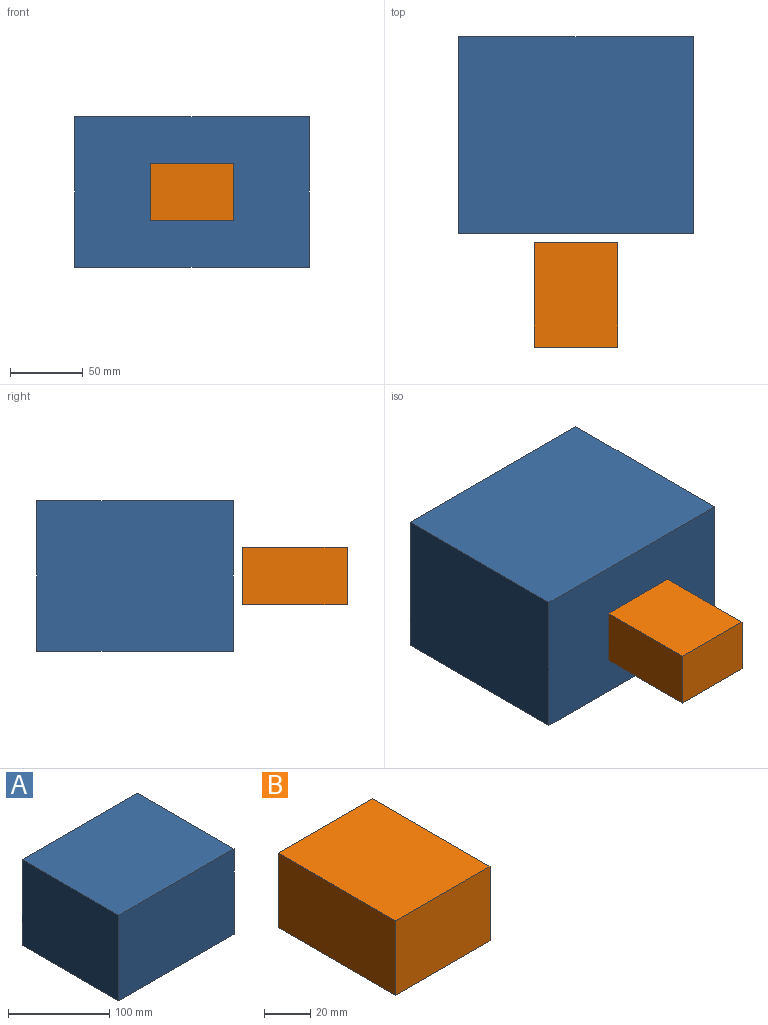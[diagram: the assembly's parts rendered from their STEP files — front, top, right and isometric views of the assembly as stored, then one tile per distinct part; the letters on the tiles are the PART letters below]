
ASSEMBLY  parts=2 mates=1
PART A: 6 faces, bbox 161x135x103.4 mm
  f0: plane 135x103.44mm, normal (1,0,0), area 13963.9mm2, adj f1,f3,f4,f5
  f1: plane 160.97x135mm, normal (0,0,1), area 21731.2mm2, adj f0,f2,f4,f5
  f2: plane 135x103.44mm, normal (-1,0,0), area 13963.9mm2, adj f1,f3,f4,f5
  f3: plane 160.97x135mm, normal (0,0,-1), area 21731.2mm2, adj f0,f2,f4,f5
  f4: plane 160.97x103.44mm, normal (0,-1,0), area 16650.3mm2, adj f0,f1,f2,f3
  f5: plane 160.97x103.44mm, normal (0,1,0), area 16650.3mm2, adj f0,f1,f2,f3
PART B: 6 faces, bbox 57.7x72x39.4 mm
  f0: plane 72x39.43mm, normal (-1,0,0), area 2838.7mm2, adj f1,f3,f4,f5
  f1: plane 72x57.67mm, normal (0,0,-1), area 4152.3mm2, adj f0,f2,f4,f5
  f2: plane 72x39.43mm, normal (1,0,0), area 2838.7mm2, adj f1,f3,f4,f5
  f3: plane 72x57.67mm, normal (0,0,1), area 4152.3mm2, adj f0,f2,f4,f5
  f4: plane 57.67x39.43mm, normal (0,-1,0), area 2273.8mm2, adj f0,f1,f2,f3
  f5: plane 57.67x39.43mm, normal (0,1,0), area 2273.8mm2, adj f0,f1,f2,f3
PLACE A t=(107.39,151.98,8.26)mm fixed
PLACE B rot(axis=(1,0,0),180deg) t=(115.72,-196.19,43.17)mm
MATE slider B.f4 <-> A.f4  axis (0,1,0) through (86.89,10.81,23.45)mm
